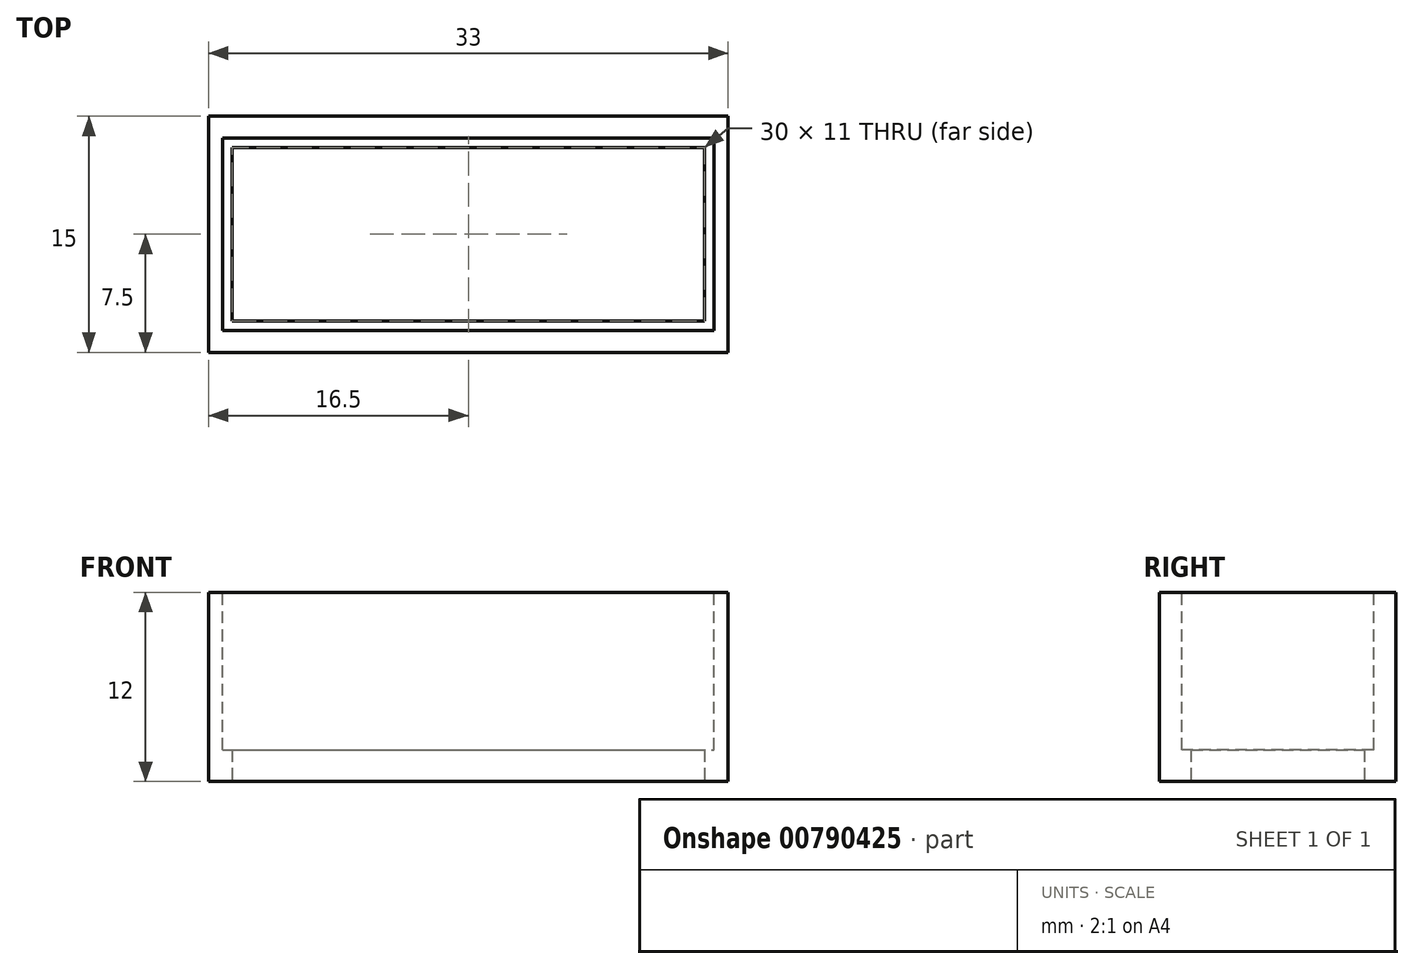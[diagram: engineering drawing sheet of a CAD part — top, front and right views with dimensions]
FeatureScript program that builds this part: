
annotation { "Feature Type Name" : "Feature", "Feature Type Description" : "" }
export const myFeature = defineFeature(function(context is Context, id is Id, definition is map)
    precondition{}
    {
        {
            var Q0;
            Q0=qCreatedBy(makeId("Top.planeOp"),FACE);
            var sketch = newSketch(context, id + "F0", { "sketchPlane" : qUnion([Q0])});
            skLineSegment(sketch, "E0.bottom", {"start": v(0, 0) * mm, "end": v(33, 0) * mm});
            skLineSegment(sketch, "E0.top", {"start": v(0, 15) * mm, "end": v(33, 15) * mm});
            skLineSegment(sketch, "E0.left", {"start": v(0, 0) * mm, "end": v(0, 15) * mm});
            skLineSegment(sketch, "E0.right", {"start": v(33, 0) * mm, "end": v(33, 15) * mm});
            skSolve(sketch);
        }
        {
            var Q0;
            Q0 = qSketchRegion(id + "F0", true);
            extrude(context, id + "F1", {"entities" : qUnion([Q0]), "depth" : 12 * mm, "offsetDistance" : 25 * mm});
        }
        {
            var Q0;
            Q0=makeQuery(id+"F1.opExtrude","CAP_FACE",FACE,{"disambiguationData":[OSD([sQuery(id+"F0.wireOp",EDGE,"E0.bottom"),sQuery(id+"F0.wireOp",EDGE,"E0.top"),sQuery(id+"F0.wireOp",EDGE,"E0.left"),sQuery(id+"F0.wireOp",EDGE,"E0.right")])],"isStart":false});
            var sketch = newSketch(context, id + "F2", { "sketchPlane" : qUnion([Q0])});
            skLineSegment(sketch, "E1.bottom", {"start": v(0.9, 13.6) * mm, "end": v(32.1, 13.6) * mm});
            skLineSegment(sketch, "E1.top", {"start": v(0.9, 1.4) * mm, "end": v(32.1, 1.4) * mm});
            skLineSegment(sketch, "E1.left", {"start": v(0.9, 13.6) * mm, "end": v(0.9, 1.4) * mm});
            skLineSegment(sketch, "E1.right", {"start": v(32.1, 13.6) * mm, "end": v(32.1, 1.4) * mm});
            skSolve(sketch);
        }
        {
            var Q0;
            Q0 = qSketchRegion(id + "F2", true);
            extrude(context, id + "F3", {"entities" : qUnion([Q0]), "operationType" : NewBodyOperationType.REMOVE, "oppositeDirection" : true, "depth" : 10 * mm, "offsetDistance" : 25 * mm});
        }
        {
            var Q0;
            Q0=makeQuery(id+"F1.opExtrude","CAP_FACE",FACE,{"disambiguationData":[OSD([sQuery(id+"F0.wireOp",EDGE,"E0.bottom"),sQuery(id+"F0.wireOp",EDGE,"E0.top"),sQuery(id+"F0.wireOp",EDGE,"E0.left"),sQuery(id+"F0.wireOp",EDGE,"E0.right")])],"isStart":true});
            var sketch = newSketch(context, id + "F4", { "sketchPlane" : qUnion([Q0])});
            skLineSegment(sketch, "E2.bottom", {"start": v(31.5, -13) * mm, "end": v(1.5, -13) * mm});
            skLineSegment(sketch, "E2.top", {"start": v(31.5, -2) * mm, "end": v(1.5, -2) * mm});
            skLineSegment(sketch, "E2.left", {"start": v(31.5, -13) * mm, "end": v(31.5, -2) * mm});
            skLineSegment(sketch, "E2.right", {"start": v(1.5, -13) * mm, "end": v(1.5, -2) * mm});
            skSolve(sketch);
        }
        {
            var Q0;
            Q0 = qSketchRegion(id + "F4", true);
            extrude(context, id + "F5", {"entities" : qUnion([Q0]), "operationType" : NewBodyOperationType.REMOVE, "endBound" : BoundingType.THROUGH_ALL, "oppositeDirection" : true, "depth" : 25 * mm, "offsetDistance" : 25 * mm});
        }
    });
